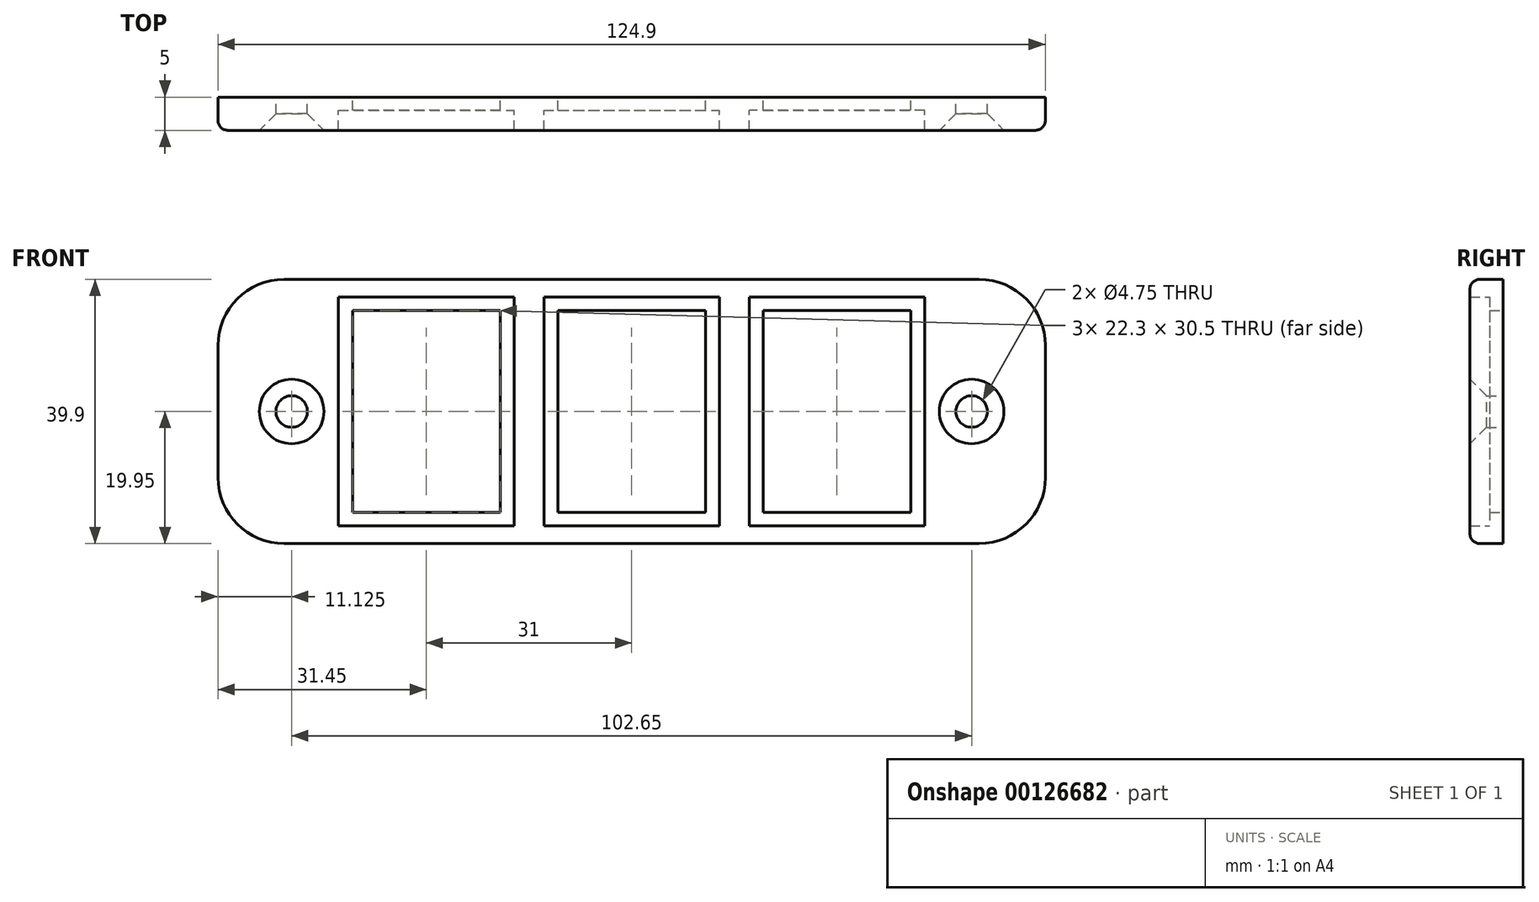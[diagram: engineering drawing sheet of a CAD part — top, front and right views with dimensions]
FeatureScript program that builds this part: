
annotation { "Feature Type Name" : "Feature", "Feature Type Description" : "" }
export const myFeature = defineFeature(function(context is Context, id is Id, definition is map)
    precondition{}
    {
        {
            var Q0;
            Q0=qCreatedBy(makeId("Front.planeOp"),FACE);
            var sketch = newSketch(context, id + "F0", { "sketchPlane" : qUnion([Q0])});
            skLineSegment(sketch, "E0.bottom", {"start": v(-52.45, 19.95) * mm, "end": v(52.45, 19.95) * mm});
            skLineSegment(sketch, "E0.top", {"start": v(-52.45, -19.95) * mm, "end": v(52.45, -19.95) * mm});
            skLineSegment(sketch, "E0.left", {"start": v(-62.45, 9.95) * mm, "end": v(-62.45, -9.95) * mm});
            skLineSegment(sketch, "E0.right", {"start": v(62.45, 9.95) * mm, "end": v(62.45, -9.95) * mm});
            skPoint(sketch, "E1.visualSharp", {"position": v(-62.45, 19.95) * mm});
            skArc(sketch, "E1.filletArc", {"start": v(-52.45, 19.95) * mm, "mid": v(-59.52, 17.02) * mm, "end": v(-62.45, 9.95) * mm});
            skPoint(sketch, "E2.visualSharp", {"position": v(62.45, 19.95) * mm});
            skArc(sketch, "E2.filletArc", {"start": v(62.45, 9.95) * mm, "mid": v(59.52, 17.02) * mm, "end": v(52.45, 19.95) * mm});
            skPoint(sketch, "E3.visualSharp", {"position": v(62.45, -19.95) * mm});
            skArc(sketch, "E3.filletArc", {"start": v(52.45, -19.95) * mm, "mid": v(59.52, -17.02) * mm, "end": v(62.45, -9.95) * mm});
            skPoint(sketch, "E4.visualSharp", {"position": v(-62.45, -19.95) * mm});
            skArc(sketch, "E4.filletArc", {"start": v(-62.45, -9.95) * mm, "mid": v(-59.52, -17.02) * mm, "end": v(-52.45, -19.95) * mm});
            skCircle(sketch, "E5", {"center": v(-51.33, 0) * mm, "radius": 2.38 * mm});
            skCircle(sketch, "E6.MirrorC", {"center": v(51.33, 0) * mm, "radius": 2.38 * mm});
            skLineSegment(sketch, "E7.bottom", {"start": v(19.85, 15.25) * mm, "end": v(42.15, 15.25) * mm});
            skLineSegment(sketch, "E7.top", {"start": v(19.85, -15.25) * mm, "end": v(42.15, -15.25) * mm});
            skLineSegment(sketch, "E7.left", {"start": v(19.85, 15.25) * mm, "end": v(19.85, -15.25) * mm});
            skLineSegment(sketch, "E7.right", {"start": v(42.15, 15.25) * mm, "end": v(42.15, -15.25) * mm});
            skLineSegment(sketch, "E8.bottom", {"start": v(-11.15, 15.25) * mm, "end": v(11.15, 15.25) * mm});
            skLineSegment(sketch, "E8.top", {"start": v(-11.15, -15.25) * mm, "end": v(11.15, -15.25) * mm});
            skLineSegment(sketch, "E8.left", {"start": v(-11.15, 15.25) * mm, "end": v(-11.15, -15.25) * mm});
            skLineSegment(sketch, "E8.right", {"start": v(11.15, 15.25) * mm, "end": v(11.15, -15.25) * mm});
            skLineSegment(sketch, "E9.MirrorCS", {"start": v(-19.85, 15.25) * mm, "end": v(-19.85, -15.25) * mm});
            skLineSegment(sketch, "E10.MirrorCS", {"start": v(-19.85, 15.25) * mm, "end": v(-42.15, 15.25) * mm});
            skLineSegment(sketch, "E11.MirrorCS", {"start": v(-42.15, 15.25) * mm, "end": v(-42.15, -15.25) * mm});
            skLineSegment(sketch, "E12.MirrorCS", {"start": v(-19.85, -15.25) * mm, "end": v(-42.15, -15.25) * mm});
            skLineSegment(sketch, "E13.bottom", {"start": v(-44.25, 17.25) * mm, "end": v(-17.75, 17.25) * mm});
            skLineSegment(sketch, "E13.top", {"start": v(-44.25, -17.25) * mm, "end": v(-17.75, -17.25) * mm});
            skLineSegment(sketch, "E13.left", {"start": v(-44.25, 17.25) * mm, "end": v(-44.25, -17.25) * mm});
            skLineSegment(sketch, "E13.right", {"start": v(-17.75, 17.25) * mm, "end": v(-17.75, -17.25) * mm});
            skLineSegment(sketch, "E14.bottom", {"start": v(-13.25, 17.25) * mm, "end": v(13.25, 17.25) * mm});
            skLineSegment(sketch, "E14.top", {"start": v(-13.25, -17.25) * mm, "end": v(13.25, -17.25) * mm});
            skLineSegment(sketch, "E14.left", {"start": v(-13.25, 17.25) * mm, "end": v(-13.25, -17.25) * mm});
            skLineSegment(sketch, "E14.right", {"start": v(13.25, 17.25) * mm, "end": v(13.25, -17.25) * mm});
            skLineSegment(sketch, "E15.MirrorCS", {"start": v(44.25, 17.25) * mm, "end": v(17.75, 17.25) * mm});
            skLineSegment(sketch, "E16.MirrorCS", {"start": v(44.25, 17.25) * mm, "end": v(44.25, -17.25) * mm});
            skLineSegment(sketch, "E17.MirrorCS", {"start": v(17.75, 17.25) * mm, "end": v(17.75, -17.25) * mm});
            skLineSegment(sketch, "E18.MirrorCS", {"start": v(44.25, -17.25) * mm, "end": v(17.75, -17.25) * mm});
            skLineSegment(sketch, "E19", {"start": v(-31, 15.25) * mm, "end": v(-31, -15.25) * mm, "construction": true});
            skSolve(sketch);
        }
        {
            var Q0;
            Q0=makeQuery(id+"F0.imprint","IMPRINT",FACE,{"disambiguationData":[TD([[makeQuery(id+"F0.imprint","IMPRINT",EDGE,{"derivedFrom":sQuery(id+"F0.wireOp",EDGE,"E0.bottom")}),-1.0]])]});
            extrude(context, id + "F1", {"entities" : qUnion([Q0]), "depth" : 5 * mm});
        }
        {
            var Q0;
            Q0=makeQuery(id+"F0.imprint","IMPRINT",FACE,{"disambiguationData":[TD([[makeQuery(id+"F0.imprint","IMPRINT",EDGE,{"derivedFrom":sQuery(id+"F0.wireOp",EDGE,"E9.MirrorCS")}),1.0]])]});
            var Q1;
            Q1=makeQuery(id+"F0.imprint","IMPRINT",FACE,{"disambiguationData":[TD([[makeQuery(id+"F0.imprint","IMPRINT",EDGE,{"derivedFrom":sQuery(id+"F0.wireOp",EDGE,"E8.bottom")}),1.0]])]});
            var Q2;
            Q2=makeQuery(id+"F0.imprint","IMPRINT",FACE,{"disambiguationData":[TD([[makeQuery(id+"F0.imprint","IMPRINT",EDGE,{"derivedFrom":sQuery(id+"F0.wireOp",EDGE,"E7.bottom")}),1.0]])]});
            extrude(context, id + "F2", {"entities" : qUnion([Q0, Q1, Q2]), "operationType" : NewBodyOperationType.ADD, "depth" : 2 * mm});
        }
        {
            var Q0;
            Q0=makeQuery(id+"F1.opExtrude","CAP_EDGE",EDGE,{"disambiguationData":[OSD([sQuery(id+"F0.wireOp",EDGE,"E0.left")])],"isStart":false});
            fillet(context, id + "F3", {"entities" : qUnion([Q0]), "radius" : 1.5 * mm, "tangentPropagation" : true, "allowEdgeOverflow" : false});
        }
        {
            var Q0;
            Q0=makeQuery(id+"F1.opExtrude","CAP_EDGE",EDGE,{"disambiguationData":[OSD([sQuery(id+"F0.wireOp",EDGE,"E5")])],"isStart":false});
            var Q1;
            Q1=makeQuery(id+"F1.opExtrude","CAP_EDGE",EDGE,{"disambiguationData":[OSD([sQuery(id+"F0.wireOp",EDGE,"E6.MirrorC")])],"isStart":false});
            chamfer(context, id + "F4", {"entities" : qUnion([Q0, Q1]), "width" : 2.5 * mm, "tangentPropagation" : true});
        }
    });
